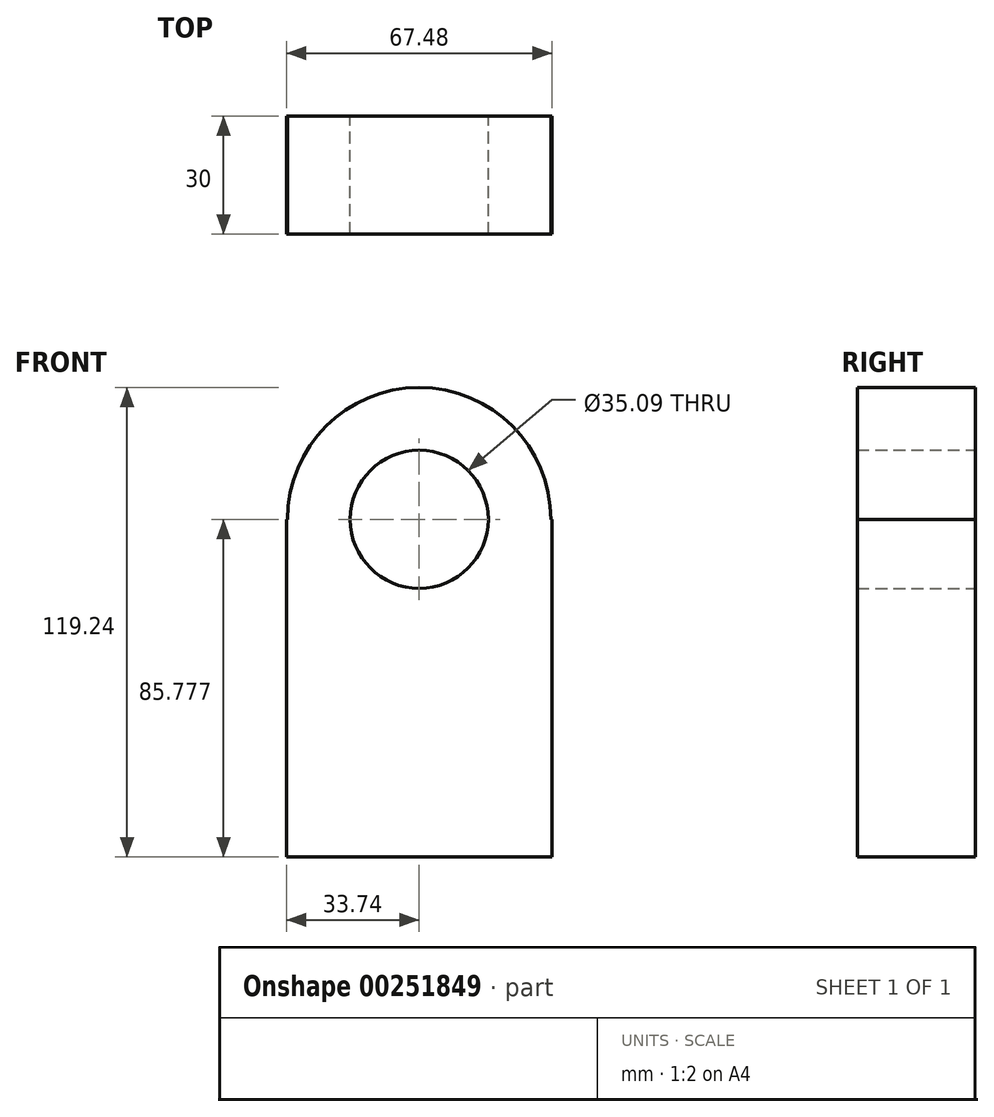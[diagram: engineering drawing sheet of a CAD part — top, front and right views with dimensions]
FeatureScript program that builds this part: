
annotation { "Feature Type Name" : "Feature", "Feature Type Description" : "" }
export const myFeature = defineFeature(function(context is Context, id is Id, definition is map)
    precondition{}
    {
        {
            var Q0;
            Q0=qCreatedBy(makeId("Front.planeOp"),FACE);
            var sketch = newSketch(context, id + "F0", { "sketchPlane" : qUnion([Q0])});
            skLineSegment(sketch, "E0", {"start": v(-33.74, 42.89) * mm, "end": v(-33.46, 42.89) * mm});
            skLineSegment(sketch, "E1", {"start": v(33.74, 42.89) * mm, "end": v(33.74, -42.89) * mm});
            skLineSegment(sketch, "E2", {"start": v(33.74, -42.89) * mm, "end": v(-33.74, -42.89) * mm});
            skLineSegment(sketch, "E3", {"start": v(-33.74, -42.89) * mm, "end": v(-33.74, 42.89) * mm});
            skArc(sketch, "E4", {"start": v(33.46, 42.89) * mm, "mid": v(0, 76.35) * mm, "end": v(-33.46, 42.89) * mm});
            skCircle(sketch, "E5", {"center": v(0, 42.89) * mm, "radius": 17.55 * mm});
            skLineSegment(sketch, "E6.trimOffspring", {"start": v(33.46, 42.89) * mm, "end": v(33.74, 42.89) * mm});
            skSolve(sketch);
        }
        {
            var Q0;
            Q0=makeQuery(id+"F0.imprint","IMPRINT",FACE,{"disambiguationData":[TD([[makeQuery(id+"F0.imprint","IMPRINT",EDGE,{"derivedFrom":sQuery(id+"F0.wireOp",EDGE,"E0")}),-1.0]])]});
            extrude(context, id + "F1", {"entities" : qUnion([Q0]), "depth" : 30 * mm});
        }
    });
